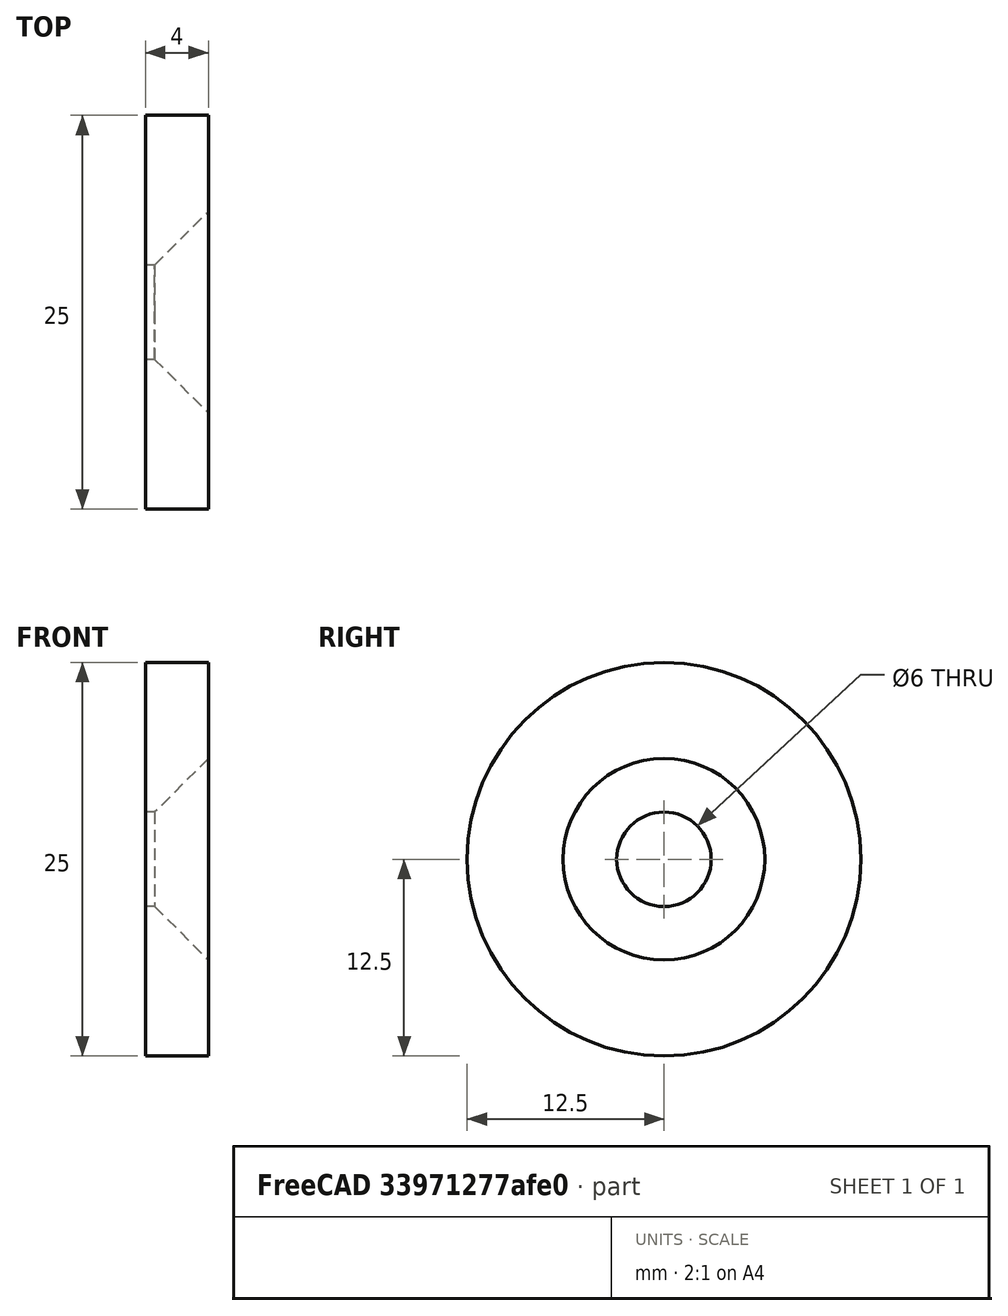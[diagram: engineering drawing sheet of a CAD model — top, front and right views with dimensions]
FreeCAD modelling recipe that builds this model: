
FCSTD DOCUMENT  (FreeCAD 0.16R5639 (Git))
Label: Washer-IV-11
License: CreativeCommons Attribution-ShareAlike
LicenseURL: http://creativecommons.org/licenses/by-sa/4.0/
objects: Sketcher::SketchObject×1, PartDesign::Revolution×1
note: 3 computed .brp shape members not serialized (recipe doc carries the construction recipe); baked Part::Feature solids carry a one-line shape summary decoded from their .brp

FEATURE [Sketcher::SketchObject] Sketch
  Placement = pos=(0,0,0) rot=(-1,0,0;4.71239rad)
  sketch-geometry (5):
    g0: LineSegment StartX=0 StartY=3 StartZ=0 EndX=0 EndY=12.5 EndZ=0
    g1: LineSegment StartX=0 StartY=12.5 StartZ=0 EndX=4 EndY=12.5 EndZ=0
    g2: LineSegment StartX=4 StartY=12.5 StartZ=0 EndX=4 EndY=6.4 EndZ=0
    g3: LineSegment StartX=4 StartY=6.4 StartZ=0 EndX=0.6 EndY=3 EndZ=0
    g4: LineSegment StartX=0.6 StartY=3 StartZ=0 EndX=0 EndY=3 EndZ=0
  constraints (15):
    c: Coincident(g0,g1)
    c: Coincident(g1,g2)
    c: Coincident(g2,g3)
    c: Coincident(g3,g4)
    c: Coincident(g0,g4)
    c: Vertical(g0)
    c: Vertical(g2)
    c: Horizontal(g4)
    c: Horizontal(g1)
    c: PointOnObject(g0,g-2)
    c: DistanceY(g-1,g1) = 12.5
    c: DistanceY(g-1,g3) = 3
    c: Angle(g2,g3) = 2.35619
    c: DistanceX(g0,g1) = 4
    c: DistanceY(g-1,g2) = 6.4
FEATURE [PartDesign::Revolution] Revolution
  Angle = 360
  Axis = (1,0,0)
  Base = (0,0,0)
  Placement = pos=(0,0,0) rot=(-1,0,0;4.71239rad)
  ReferenceAxis = -> Sketch [H_Axis]
  Sketch = -> Sketch
